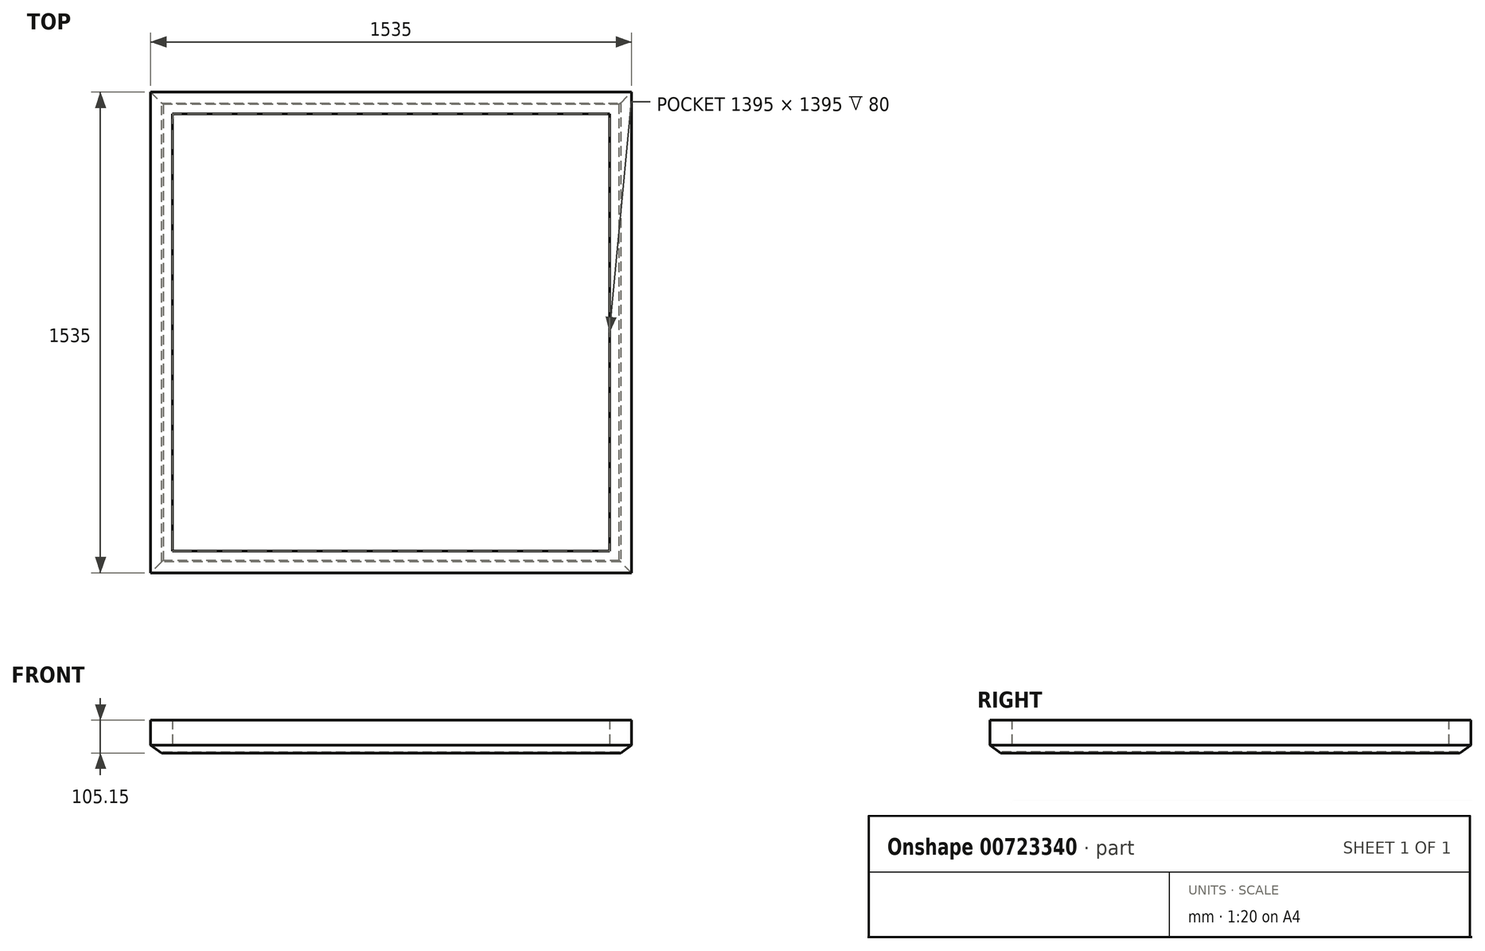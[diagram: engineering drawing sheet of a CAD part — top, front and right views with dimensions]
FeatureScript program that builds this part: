
annotation { "Feature Type Name" : "Feature", "Feature Type Description" : "" }
export const myFeature = defineFeature(function(context is Context, id is Id, definition is map)
    precondition{}
    {
        {
            var Q0;
            Q0=qCreatedBy(makeId("Top.planeOp"),FACE);
            var sketch = newSketch(context, id + "F0", { "sketchPlane" : qUnion([Q0])});
            skLineSegment(sketch, "E0.bottom", {"start": v(-767.5, 767.5) * mm, "end": v(767.5, 767.5) * mm});
            skLineSegment(sketch, "E0.top", {"start": v(-767.5, -767.5) * mm, "end": v(767.5, -767.5) * mm});
            skLineSegment(sketch, "E0.left", {"start": v(-767.5, 767.5) * mm, "end": v(-767.5, -767.5) * mm});
            skLineSegment(sketch, "E0.right", {"start": v(767.5, 767.5) * mm, "end": v(767.5, -767.5) * mm});
            skPoint(sketch, "E0.middle", {"position": v(0, 0) * mm});
            skLineSegment(sketch, "E1.bottom", {"start": v(-697.5, 697.5) * mm, "end": v(697.5, 697.5) * mm});
            skLineSegment(sketch, "E1.top", {"start": v(-697.5, -697.5) * mm, "end": v(697.5, -697.5) * mm});
            skLineSegment(sketch, "E1.left", {"start": v(-697.5, 697.5) * mm, "end": v(-697.5, -697.5) * mm});
            skLineSegment(sketch, "E1.right", {"start": v(697.5, 697.5) * mm, "end": v(697.5, -697.5) * mm});
            skSolve(sketch);
        }
        {
            var Q0;
            Q0 = qSketchRegion(id + "F0", true);
            extrude(context, id + "F1", {"entities" : qUnion([Q0]), "depth" : 80 * mm, "offsetDistance" : 25 * mm});
        }
        {
            var Q0;
            Q0=makeQuery(id+"F1.opExtrude","CAP_FACE",FACE,{"disambiguationData":[OSD([sQuery(id+"F0.wireOp",EDGE,"E0.bottom"),sQuery(id+"F0.wireOp",EDGE,"E0.top"),sQuery(id+"F0.wireOp",EDGE,"E0.left"),sQuery(id+"F0.wireOp",EDGE,"E0.right"),sQuery(id+"F0.wireOp",EDGE,"E1.bottom"),sQuery(id+"F0.wireOp",EDGE,"E1.top"),sQuery(id+"F0.wireOp",EDGE,"E1.left"),sQuery(id+"F0.wireOp",EDGE,"E1.right")])],"isStart":true});
            extrude(context, id + "F2", {"entities" : qUnion([Q0]), "operationType" : NewBodyOperationType.ADD, "depth" : 115 * mm, "offsetDistance" : 25 * mm, "hasDraft" : true, "draftAngle" : 54.3 * degree, "draftPullDirection" : true});
        }
        {
            var Q0;
            Q0=qCreatedBy(makeId("Top.planeOp"),FACE);
            var sketch = newSketch(context, id + "F3", { "sketchPlane" : qUnion([Q0])});
            skLineSegment(sketch, "E2.bottom", {"start": v(-733.9, -729.2) * mm, "end": v(733.9, -729.2) * mm});
            skLineSegment(sketch, "E2.top", {"start": v(-733.9, 729.2) * mm, "end": v(733.9, 729.2) * mm});
            skLineSegment(sketch, "E2.left", {"start": v(-733.9, -729.2) * mm, "end": v(-733.9, 729.2) * mm});
            skLineSegment(sketch, "E2.right", {"start": v(733.9, -729.2) * mm, "end": v(733.9, 729.2) * mm});
            skPoint(sketch, "E2.middle", {"position": v(0, 0) * mm});
            skSolve(sketch);
        }
        {
            var Q0;
            Q0=makeQuery(id+"F3.imprint","IMPRINT",FACE,{"disambiguationData":[TD([[makeQuery(id+"F3.imprint","IMPRINT",EDGE,{"derivedFrom":sQuery(id+"F3.wireOp",EDGE,"E2.bottom")}),1.0]])]});
            extrude(context, id + "F4", {"entities" : qUnion([Q0]), "operationType" : NewBodyOperationType.ADD, "oppositeDirection" : true, "depth" : 21.7 * mm, "offsetDistance" : 25 * mm});
        }
    });
